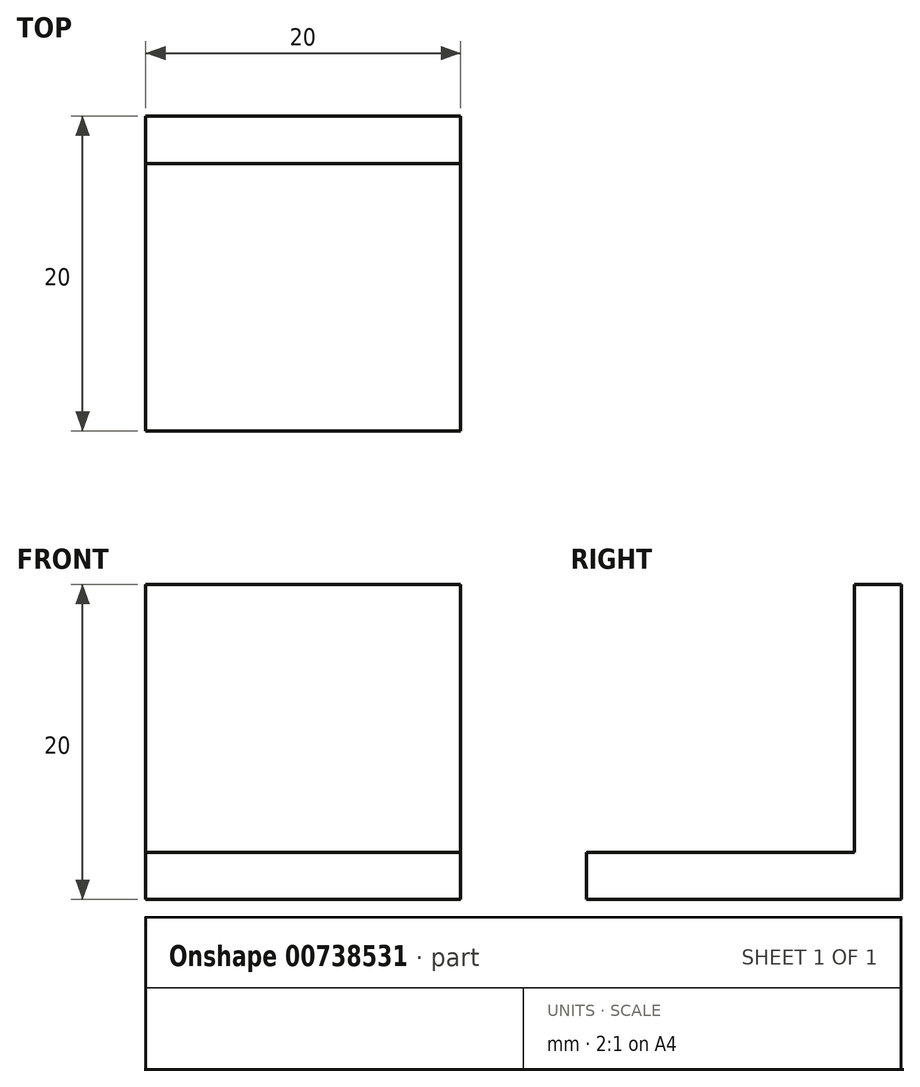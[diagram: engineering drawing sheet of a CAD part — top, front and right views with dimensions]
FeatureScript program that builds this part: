
annotation { "Feature Type Name" : "Feature", "Feature Type Description" : "" }
export const myFeature = defineFeature(function(context is Context, id is Id, definition is map)
    precondition{}
    {
        {
            var Q0;
            Q0=qCreatedBy(makeId("Top.planeOp"),FACE);
            var sketch = newSketch(context, id + "F0", { "sketchPlane" : qUnion([Q0])});
            skLineSegment(sketch, "E0.bottom", {"start": v(0, 0) * mm, "end": v(20, 0) * mm});
            skLineSegment(sketch, "E0.top", {"start": v(0, 20) * mm, "end": v(20, 20) * mm});
            skLineSegment(sketch, "E0.left", {"start": v(0, 0) * mm, "end": v(0, 20) * mm});
            skLineSegment(sketch, "E0.right", {"start": v(20, 0) * mm, "end": v(20, 20) * mm});
            skLineSegment(sketch, "E1.left", {"start": v(0, 20) * mm, "end": v(0, 17) * mm});
            skLineSegment(sketch, "E1.right", {"start": v(20, 20) * mm, "end": v(20, 17) * mm});
            skSolve(sketch);
        }
        {
            var Q0;
            Q0=makeQuery(id+"F0.imprint","IMPRINT",FACE,{"disambiguationData":[TD([[makeQuery(id+"F0.imprint","IMPRINT",EDGE,{"derivedFrom":sQuery(id+"F0.wireOp",EDGE,"E0.bottom")}),1.0]])]});
            extrude(context, id + "F1", {"entities" : qUnion([Q0]), "depth" : 3 * mm, "offsetDistance" : 25 * mm});
        }
        {
            var Q0;
            Q0=makeQuery(id+"F1.opExtrude","CAP_FACE",FACE,{"disambiguationData":[OSD([sQuery(id+"F0.wireOp",EDGE,"E0.bottom"),sQuery(id+"F0.wireOp",EDGE,"E0.left"),sQuery(id+"F0.wireOp",EDGE,"E0.right"),sQuery(id+"F0.wireOp",EDGE,"E1.top")])],"isStart":false});
            var sketch = newSketch(context, id + "F2", { "sketchPlane" : qUnion([Q0])});
            skLineSegment(sketch, "E2.bottom", {"start": v(0, 20) * mm, "end": v(20, 20) * mm});
            skLineSegment(sketch, "E2.left", {"start": v(0, 20) * mm, "end": v(0, 17) * mm});
            skLineSegment(sketch, "E2.right", {"start": v(20, 20) * mm, "end": v(20, 17) * mm});
            skLineSegment(sketch, "E3", {"start": v(0, 17) * mm, "end": v(20, 17) * mm});
            skSolve(sketch);
        }
        {
            var Q0;
            Q0=makeQuery(id+"F2.imprint","IMPRINT",FACE,{"disambiguationData":[TD([[makeQuery(id+"F2.imprint","IMPRINT",EDGE,{"derivedFrom":sQuery(id+"F2.wireOp",EDGE,"E2.bottom")}),-1.0]])]});
            extrude(context, id + "F3", {"entities" : qUnion([Q0]), "operationType" : NewBodyOperationType.ADD, "depth" : 17 * mm, "offsetDistance" : 25 * mm});
        }
    });
